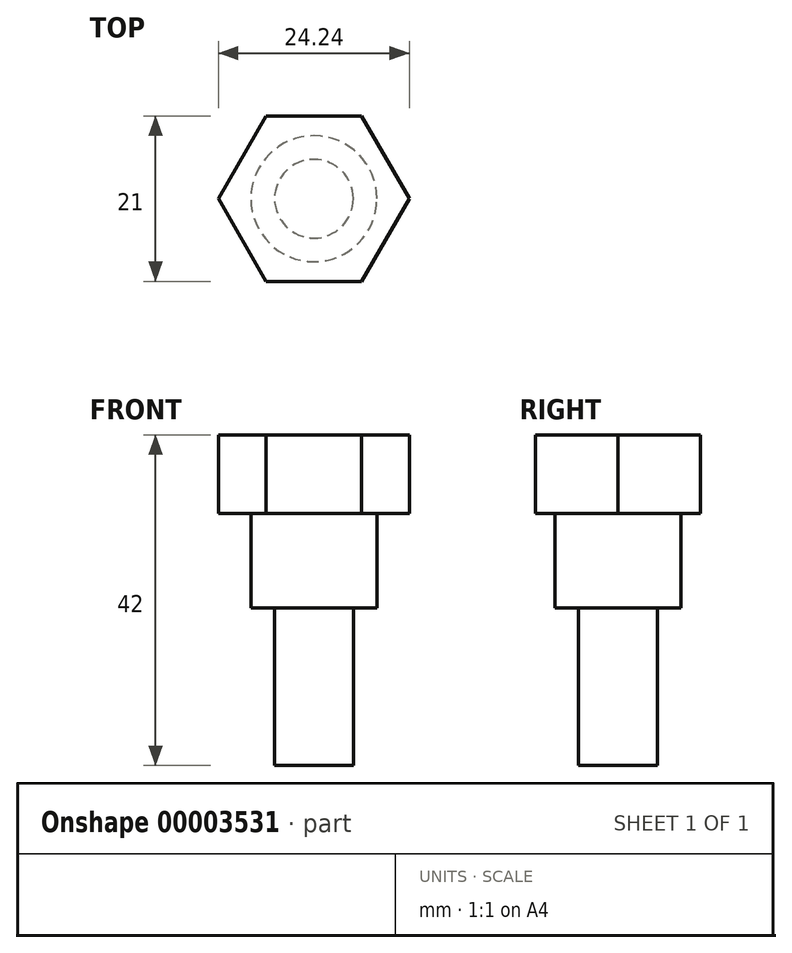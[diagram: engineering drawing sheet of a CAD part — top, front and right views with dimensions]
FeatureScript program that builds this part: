
annotation { "Feature Type Name" : "Feature", "Feature Type Description" : "" }
export const myFeature = defineFeature(function(context is Context, id is Id, definition is map)
    precondition{}
    {
        {
            var Q0;
            Q0=qCreatedBy(makeId("Right.planeOp"),FACE);
            var sketch = newSketch(context, id + "F0", { "sketchPlane" : qUnion([Q0])});
            skLineSegment(sketch, "E0", {"start": v(0, 0) * mm, "end": v(0, 32) * mm});
            skLineSegment(sketch, "E1", {"start": v(0, 32) * mm, "end": v(8, 32) * mm});
            skLineSegment(sketch, "E2", {"start": v(8, 32) * mm, "end": v(8, 20) * mm});
            skLineSegment(sketch, "E3", {"start": v(8, 20) * mm, "end": v(5, 20) * mm});
            skLineSegment(sketch, "E4", {"start": v(5, 20) * mm, "end": v(5, 0) * mm});
            skLineSegment(sketch, "E5", {"start": v(5, 0) * mm, "end": v(0, 0) * mm});
            skSolve(sketch);
        }
        {
            var Q0;
            Q0=makeQuery(id+"F0.imprint","IMPRINT",FACE,{"disambiguationData":[TD([[makeQuery(id+"F0.imprint","IMPRINT",EDGE,{"derivedFrom":sQuery(id+"F0.wireOp",EDGE,"E0")}),-1.0]])]});
            var Q1;
            Q1=sQuery(id+"F0.wireOp",EDGE,"E0");
            revolve(context, id + "F1", {"entities" : qUnion([Q0]), "axis" : qUnion([Q1]), "revolveType" : RevolveType.FULL});
        }
        {
            var Q0;
            Q0=makeQuery(id+"F1.opRevolve","SWEPT_FACE",FACE,{"disambiguationData":[OSD([sQuery(id+"F0.wireOp",EDGE,"E1")])]});
            var sketch = newSketch(context, id + "F2", { "sketchPlane" : qUnion([Q0])});
            skCircle(sketch, "E6.cCircle", {"center": v(0, 0) * mm, "radius": 10.5 * mm, "construction": true});
            skLineSegment(sketch, "E6.0", {"start": v(-6.06, 10.5) * mm, "end": v(6.06, 10.5) * mm});
            skLineSegment(sketch, "E6.1", {"start": v(6.06, 10.5) * mm, "end": v(12.12, 0) * mm});
            skLineSegment(sketch, "E6.2", {"start": v(12.12, 0) * mm, "end": v(6.06, -10.5) * mm});
            skLineSegment(sketch, "E6.3", {"start": v(6.06, -10.5) * mm, "end": v(-6.06, -10.5) * mm});
            skLineSegment(sketch, "E6.4", {"start": v(-6.06, -10.5) * mm, "end": v(-12.12, 0) * mm});
            skLineSegment(sketch, "E6.5", {"start": v(-12.12, 0) * mm, "end": v(-6.06, 10.5) * mm});
            skPoint(sketch, "E6.0.midPoint", {"position": v(0, 10.5) * mm});
            skSolve(sketch);
        }
        {
            var Q0;
            Q0=makeQuery(id+"F2.imprint","IMPRINT",FACE,{"disambiguationData":[TD([[makeQuery(id+"F2.imprint","IMPRINT",EDGE,{"derivedFrom":makeQuery(id+"F1.opRevolve","SWEPT_EDGE",EDGE,{"disambiguationData":[OSD([sQuery(id+"F0.wireOp",EDGE,"E1"),sQuery(id+"F0.wireOp",EDGE,"E2")])]})}),-1.0]])]});
            var Q1;
            Q1=makeQuery(id+"F2.imprint","IMPRINT",FACE,{"disambiguationData":[TD([[makeQuery(id+"F2.imprint","IMPRINT",EDGE,{"derivedFrom":sQuery(id+"F2.wireOp",EDGE,"E6.0")}),-1.0]])]});
            extrude(context, id + "F3", {"entities" : qUnion([Q0, Q1]), "operationType" : NewBodyOperationType.ADD, "depth" : 10 * mm});
        }
    });
